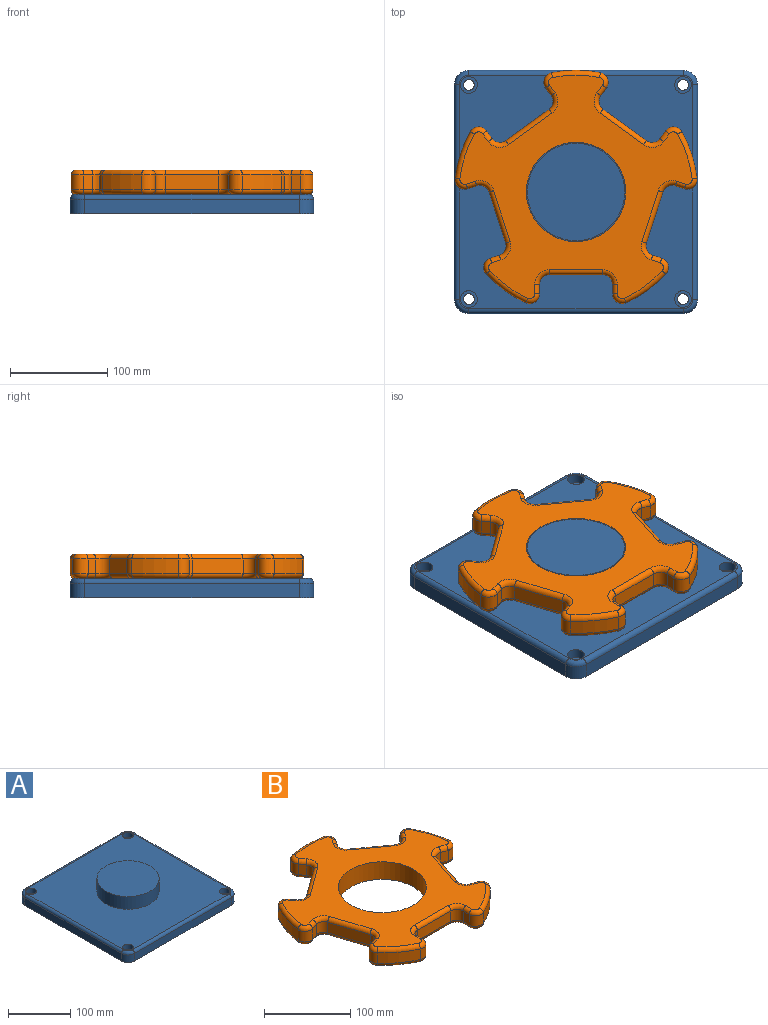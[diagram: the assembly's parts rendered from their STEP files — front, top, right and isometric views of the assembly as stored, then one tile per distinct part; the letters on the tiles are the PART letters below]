
ASSEMBLY  parts=2 mates=1
PART A: 32 faces, bbox 252.5x252.5x45 mm
  f0: plane 220x15mm, normal (1,0,0), area 3300mm2, adj f5,f8,f11,f27
  f1: plane 220x15mm, normal (0,1,0), area 3300mm2, adj f5,f8,f9,f31
  f2: plane 220x15mm, normal (-1,0,0), area 3300mm2, adj f5,f9,f10,f28
  f3: plane 220x15mm, normal (0,-1,0), area 3300mm2, adj f5,f10,f11,f24
  f4: plane 240x240mm, normal (0,0,1), area 48725.4mm2, adj f6,f14,f17,f20,f23,f24,f25,f26
  f5: plane 250x250mm, normal (0,0,-1), area 61926.7mm2, adj f0,f1,f2,f3,f8,f9,f10,f11
  f6: cylinder r=50mm len=100mm, axis (0,0,-1), area 7854mm2, adj f4,f7
  f7: plane 100x100mm, normal (0,0,1), area 7854mm2, adj f6
  f8: cylinder r=15mm len=15mm, axis (0,0,-1), area 353.4mm2, adj f0,f1,f5,f29
  f9: cylinder r=15mm len=15mm, axis (0,0,1), area 353.4mm2, adj f1,f2,f5,f30
  f10: cylinder r=15mm len=15mm, axis (0,0,-1), area 353.4mm2, adj f2,f3,f5,f26
  f11: cylinder r=15mm len=15mm, axis (0,0,1), area 353.4mm2, adj f0,f3,f5,f25
  f12: cylinder r=5.5mm len=11mm, axis (0,0,1), area 345.6mm2, adj f5,f13
  f13: plane 17.25x17.25mm, normal (0,0,1), area 138.7mm2, adj f12,f14
  f14: cylinder r=8.62mm len=17.25mm, axis (0,0,1), area 541.9mm2, adj f4,f13
  f15: cylinder r=5.5mm len=11mm, axis (0,0,1), area 345.6mm2, adj f5,f16
  f16: plane 17.25x17.25mm, normal (0,0,1), area 138.7mm2, adj f15,f17
  f17: cylinder r=8.62mm len=17.25mm, axis (0,0,1), area 541.9mm2, adj f4,f16
  f18: cylinder r=5.5mm len=11mm, axis (0,0,1), area 345.6mm2, adj f5,f19
  f19: plane 17.25x17.25mm, normal (0,0,1), area 138.7mm2, adj f18,f20
  f20: cylinder r=8.62mm len=17.25mm, axis (0,0,1), area 541.9mm2, adj f4,f19
  f21: cylinder r=5.5mm len=11mm, axis (0,0,1), area 345.6mm2, adj f5,f22
  f22: plane 17.25x17.25mm, normal (0,0,1), area 138.7mm2, adj f21,f23
  f23: cylinder r=8.62mm len=17.25mm, axis (0,0,1), area 541.9mm2, adj f4,f22
  f24: cylinder r=5mm len=220mm, axis (-1,0,0), area 1727.9mm2, adj f3,f4,f25,f26
  f25: torus R=10mm, axis (0,0,1), area 162.6mm2, adj f4,f11,f24,f27
  f26: torus R=10mm, axis (0,0,1), area 162.6mm2, adj f4,f10,f24,f28
  f27: cylinder r=5mm len=220mm, axis (0,-1,0), area 1727.9mm2, adj f0,f4,f25,f29
  f28: cylinder r=5mm len=220mm, axis (0,1,0), area 1727.9mm2, adj f2,f4,f26,f30
  f29: torus R=10mm, axis (0,0,1), area 162.6mm2, adj f4,f8,f27,f31
  f30: torus R=10mm, axis (0,0,1), area 162.6mm2, adj f4,f9,f28,f31
  f31: cylinder r=5mm len=220mm, axis (1,0,0), area 1727.9mm2, adj f1,f4,f29,f30
PART B: 123 faces, bbox 268.9x258.5x25 mm
  f0: plane 238.57x229.73mm, normal (0,0,1), area 21505.7mm2, adj f6,f43,f44,f45,f46,f47,f48,f49
  f1: plane 238.57x229.73mm, normal (0,0,-1), area 21505.7mm2, adj f6,f83,f84,f85,f86,f87,f88,f89
  f2: cylinder r=125mm len=40.68mm, axis (0,0,-1), area 759.5mm2, adj f13,f42,f51,f91
  f3: cylinder r=125mm len=47.82mm, axis (0,0,-1), area 759.5mm2, adj f35,f41,f67,f107
  f4: cylinder r=125mm len=50.29mm, axis (0,0,-1), area 759.5mm2, adj f28,f34,f82,f122
  f5: cylinder r=125mm len=47.82mm, axis (0,0,-1), area 759.5mm2, adj f21,f27,f66,f106
  f6: cylinder r=51mm len=102mm, axis (0,0,-1), area 8011.1mm2, adj f0,f1
  f7: cylinder r=125mm len=40.68mm, axis (0,0,-1), area 759.5mm2, adj f14,f20,f50,f90
  f8: plane 15x9.73mm, normal (-1,0,0), area 146mm2, adj f11,f14,f46,f86
  f9: plane 55x15mm, normal (0,-1,0), area 825mm2, adj f11,f12,f43,f83
  f10: plane 15x9.73mm, normal (1,0,0), area 146mm2, adj f12,f13,f47,f87
  f11: cylinder r=10mm len=15mm, axis (0,0,-1), area 235.6mm2, adj f8,f9,f44,f84
  f12: cylinder r=10mm len=15mm, axis (0,0,-1), area 235.6mm2, adj f9,f10,f45,f85
  f13: cylinder r=10mm len=15mm, axis (0,0,-1), area 299.5mm2, adj f2,f10,f49,f89
  f14: cylinder r=10mm len=15mm, axis (0,0,-1), area 299.5mm2, adj f7,f8,f48,f88
  f15: plane 15x9.26mm, normal (-0.31,-0.95,0), area 146mm2, adj f18,f21,f62,f102
  f16: plane 52.31x17mm, normal (0.95,-0.31,0), area 825mm2, adj f18,f19,f58,f98
  f17: plane 15x9.26mm, normal (0.31,0.95,0), area 146mm2, adj f19,f20,f54,f94
  f18: cylinder r=10mm len=15mm, axis (0,0,-1), area 235.6mm2, adj f15,f16,f60,f100
  f19: cylinder r=10mm len=15mm, axis (0,0,-1), area 235.6mm2, adj f16,f17,f56,f96
  f20: cylinder r=10mm len=16.25mm, axis (0,0,-1), area 299.5mm2, adj f7,f17,f52,f92
  f21: cylinder r=10mm len=15mm, axis (0,0,-1), area 299.5mm2, adj f5,f15,f64,f104
  f22: plane 15x7.87mm, normal (0.81,-0.59,0), area 146mm2, adj f25,f28,f78,f118
  f23: plane 44.5x32.33mm, normal (0.59,0.81,0), area 825mm2, adj f25,f26,f74,f114
  f24: plane 15x7.87mm, normal (-0.81,0.59,0), area 146mm2, adj f26,f27,f70,f110
  f25: cylinder r=10mm len=15mm, axis (0,0,-1), area 235.6mm2, adj f22,f23,f76,f116
  f26: cylinder r=10mm len=15mm, axis (0,0,-1), area 235.6mm2, adj f23,f24,f72,f112
  f27: cylinder r=10mm len=16.78mm, axis (0,0,-1), area 299.5mm2, adj f5,f24,f68,f108
  f28: cylinder r=10mm len=15.67mm, axis (0,0,-1), area 299.5mm2, adj f4,f22,f80,f120
  f29: plane 15x7.87mm, normal (0.81,0.59,0), area 146mm2, adj f32,f35,f71,f111
  f30: plane 44.5x32.33mm, normal (-0.59,0.81,0), area 825mm2, adj f32,f33,f75,f115
  f31: plane 15x7.87mm, normal (-0.81,-0.59,0), area 146mm2, adj f33,f34,f79,f119
  f32: cylinder r=10mm len=15mm, axis (0,0,-1), area 235.6mm2, adj f29,f30,f73,f113
  f33: cylinder r=10mm len=15mm, axis (0,0,-1), area 235.6mm2, adj f30,f31,f77,f117
  f34: cylinder r=10mm len=15.67mm, axis (0,0,-1), area 299.5mm2, adj f4,f31,f81,f121
  f35: cylinder r=10mm len=16.78mm, axis (0,0,-1), area 299.5mm2, adj f3,f29,f69,f109
  f36: plane 15x9.26mm, normal (-0.31,0.95,0), area 146mm2, adj f39,f42,f55,f95
  f37: plane 52.31x17mm, normal (-0.95,-0.31,0), area 825mm2, adj f39,f40,f59,f99
  f38: plane 15x9.26mm, normal (0.31,-0.95,0), area 146mm2, adj f40,f41,f63,f103
  f39: cylinder r=10mm len=15mm, axis (0,0,-1), area 235.6mm2, adj f36,f37,f57,f97
  f40: cylinder r=10mm len=15mm, axis (0,0,-1), area 235.6mm2, adj f37,f38,f61,f101
  f41: cylinder r=10mm len=15mm, axis (0,0,-1), area 299.5mm2, adj f3,f38,f65,f105
  f42: cylinder r=10mm len=16.25mm, axis (0,0,-1), area 299.5mm2, adj f2,f36,f53,f93
  f43: cylinder r=5mm len=55mm, axis (1,0,0), area 432mm2, adj f0,f9,f44,f45
  f44: torus R=15mm, axis (0,0,1), area 145.8mm2, adj f0,f11,f43,f46
  f45: torus R=15mm, axis (0,0,1), area 145.8mm2, adj f0,f12,f43,f47
  f46: cylinder r=5mm len=9.73mm, axis (0,-1,0), area 76.4mm2, adj f0,f8,f44,f48
  f47: cylinder r=5mm len=9.73mm, axis (0,1,0), area 76.4mm2, adj f0,f10,f45,f49
  f48: torus R=5mm, axis (0,0,1), area 128.3mm2, adj f0,f14,f46,f50
  f49: torus R=5mm, axis (0,0,1), area 128.3mm2, adj f0,f13,f47,f51
  f50: torus R=120mm, axis (0,0,1), area 391.9mm2, adj f0,f7,f48,f52
  f51: torus R=120mm, axis (0,0,1), area 391.9mm2, adj f0,f2,f49,f53
  f52: torus R=5mm, axis (0,0,1), area 128.3mm2, adj f0,f20,f50,f54
  f53: torus R=5mm, axis (0,0,1), area 128.3mm2, adj f0,f42,f51,f55
  f54: cylinder r=5mm len=10.8mm, axis (-0.95,0.31,0), area 76.4mm2, adj f0,f17,f52,f56
  f55: cylinder r=5mm len=10.8mm, axis (-0.95,-0.31,0), area 76.4mm2, adj f0,f36,f53,f57
  f56: torus R=15mm, axis (0,0,1), area 145.8mm2, adj f0,f19,f54,f58
  f57: torus R=15mm, axis (0,0,1), area 145.8mm2, adj f0,f39,f55,f59
  f58: cylinder r=5mm len=53.85mm, axis (0.31,0.95,0), area 432mm2, adj f0,f16,f56,f60
  f59: cylinder r=5mm len=53.85mm, axis (0.31,-0.95,0), area 432mm2, adj f0,f37,f57,f61
  f60: torus R=15mm, axis (0,0,1), area 145.8mm2, adj f0,f18,f58,f62
  f61: torus R=15mm, axis (0,0,1), area 145.8mm2, adj f0,f40,f59,f63
  f62: cylinder r=5mm len=10.8mm, axis (0.95,-0.31,0), area 76.4mm2, adj f0,f15,f60,f64
  f63: cylinder r=5mm len=10.8mm, axis (0.95,0.31,0), area 76.4mm2, adj f0,f38,f61,f65
  f64: torus R=5mm, axis (0,0,1), area 128.3mm2, adj f0,f21,f62,f66
  f65: torus R=5mm, axis (0,0,1), area 128.3mm2, adj f0,f41,f63,f67
  f66: torus R=120mm, axis (0,0,1), area 391.9mm2, adj f0,f5,f64,f68
  f67: torus R=120mm, axis (0,0,1), area 391.9mm2, adj f0,f3,f65,f69
  f68: torus R=5mm, axis (0,0,1), area 128.3mm2, adj f0,f27,f66,f70
  f69: torus R=5mm, axis (0,0,1), area 128.3mm2, adj f0,f35,f67,f71
  f70: cylinder r=5mm len=10.81mm, axis (-0.59,-0.81,0), area 76.4mm2, adj f0,f24,f68,f72
  f71: cylinder r=5mm len=10.81mm, axis (-0.59,0.81,0), area 76.4mm2, adj f0,f29,f69,f73
  f72: torus R=15mm, axis (0,0,1), area 145.8mm2, adj f0,f26,f70,f74
  f73: torus R=15mm, axis (0,0,1), area 145.8mm2, adj f0,f32,f71,f75
  f74: cylinder r=5mm len=47.44mm, axis (-0.81,0.59,0), area 432mm2, adj f0,f23,f72,f76
  f75: cylinder r=5mm len=47.44mm, axis (-0.81,-0.59,0), area 432mm2, adj f0,f30,f73,f77
  f76: torus R=15mm, axis (0,0,1), area 145.8mm2, adj f0,f25,f74,f78
  f77: torus R=15mm, axis (0,0,1), area 145.8mm2, adj f0,f33,f75,f79
  f78: cylinder r=5mm len=10.81mm, axis (0.59,0.81,0), area 76.4mm2, adj f0,f22,f76,f80
  f79: cylinder r=5mm len=10.81mm, axis (0.59,-0.81,0), area 76.4mm2, adj f0,f31,f77,f81
  f80: torus R=5mm, axis (0,0,1), area 128.3mm2, adj f0,f28,f78,f82
  f81: torus R=5mm, axis (0,0,1), area 128.3mm2, adj f0,f34,f79,f82
  f82: torus R=120mm, axis (0,0,1), area 391.9mm2, adj f0,f4,f80,f81
  f83: cylinder r=5mm len=55mm, axis (-1,0,0), area 432mm2, adj f1,f9,f84,f85
  f84: torus R=15mm, axis (0,0,1), area 145.8mm2, adj f1,f11,f83,f86
  f85: torus R=15mm, axis (0,0,1), area 145.8mm2, adj f1,f12,f83,f87
  f86: cylinder r=5mm len=9.73mm, axis (0,1,0), area 76.4mm2, adj f1,f8,f84,f88
  f87: cylinder r=5mm len=9.73mm, axis (0,-1,0), area 76.4mm2, adj f1,f10,f85,f89
  f88: torus R=5mm, axis (0,0,1), area 128.3mm2, adj f1,f14,f86,f90
  f89: torus R=5mm, axis (0,0,1), area 128.3mm2, adj f1,f13,f87,f91
  f90: torus R=120mm, axis (0,0,1), area 391.9mm2, adj f1,f7,f88,f92
  f91: torus R=120mm, axis (0,0,1), area 391.9mm2, adj f1,f2,f89,f93
  f92: torus R=5mm, axis (0,0,1), area 128.3mm2, adj f1,f20,f90,f94
  f93: torus R=5mm, axis (0,0,1), area 128.3mm2, adj f1,f42,f91,f95
  f94: cylinder r=5mm len=10.8mm, axis (0.95,-0.31,0), area 76.4mm2, adj f1,f17,f92,f96
  f95: cylinder r=5mm len=10.8mm, axis (0.95,0.31,0), area 76.4mm2, adj f1,f36,f93,f97
  f96: torus R=15mm, axis (0,0,1), area 145.8mm2, adj f1,f19,f94,f98
  f97: torus R=15mm, axis (0,0,1), area 145.8mm2, adj f1,f39,f95,f99
  f98: cylinder r=5mm len=53.85mm, axis (-0.31,-0.95,0), area 432mm2, adj f1,f16,f96,f100
  f99: cylinder r=5mm len=53.85mm, axis (-0.31,0.95,0), area 432mm2, adj f1,f37,f97,f101
  f100: torus R=15mm, axis (0,0,1), area 145.8mm2, adj f1,f18,f98,f102
  f101: torus R=15mm, axis (0,0,1), area 145.8mm2, adj f1,f40,f99,f103
  f102: cylinder r=5mm len=10.8mm, axis (-0.95,0.31,0), area 76.4mm2, adj f1,f15,f100,f104
  f103: cylinder r=5mm len=10.8mm, axis (-0.95,-0.31,0), area 76.4mm2, adj f1,f38,f101,f105
  f104: torus R=5mm, axis (0,0,1), area 128.3mm2, adj f1,f21,f102,f106
  f105: torus R=5mm, axis (0,0,1), area 128.3mm2, adj f1,f41,f103,f107
  f106: torus R=120mm, axis (0,0,1), area 391.9mm2, adj f1,f5,f104,f108
  f107: torus R=120mm, axis (0,0,1), area 391.9mm2, adj f1,f3,f105,f109
  f108: torus R=5mm, axis (0,0,1), area 128.3mm2, adj f1,f27,f106,f110
  f109: torus R=5mm, axis (0,0,1), area 128.3mm2, adj f1,f35,f107,f111
  f110: cylinder r=5mm len=10.81mm, axis (0.59,0.81,0), area 76.4mm2, adj f1,f24,f108,f112
  f111: cylinder r=5mm len=10.81mm, axis (0.59,-0.81,0), area 76.4mm2, adj f1,f29,f109,f113
  f112: torus R=15mm, axis (0,0,1), area 145.8mm2, adj f1,f26,f110,f114
  f113: torus R=15mm, axis (0,0,1), area 145.8mm2, adj f1,f32,f111,f115
  f114: cylinder r=5mm len=47.44mm, axis (0.81,-0.59,0), area 432mm2, adj f1,f23,f112,f116
  f115: cylinder r=5mm len=47.44mm, axis (0.81,0.59,0), area 432mm2, adj f1,f30,f113,f117
  f116: torus R=15mm, axis (0,0,1), area 145.8mm2, adj f1,f25,f114,f118
  f117: torus R=15mm, axis (0,0,1), area 145.8mm2, adj f1,f33,f115,f119
  f118: cylinder r=5mm len=10.81mm, axis (-0.59,-0.81,0), area 76.4mm2, adj f1,f22,f116,f120
  f119: cylinder r=5mm len=10.81mm, axis (-0.59,0.81,0), area 76.4mm2, adj f1,f31,f117,f121
  f120: torus R=5mm, axis (0,0,1), area 128.3mm2, adj f1,f28,f118,f122
  f121: torus R=5mm, axis (0,0,1), area 128.3mm2, adj f1,f34,f119,f122
  f122: torus R=120mm, axis (0,0,1), area 391.9mm2, adj f1,f4,f120,f121
PLACE A t=(-21.37,22.92,28.1)mm
PLACE B t=(-21.37,22.92,28.1)mm
MATE revolute A.f6 <-> B.f2  axis (0,0,1) through (-21.37,22.92,73.1)mm
